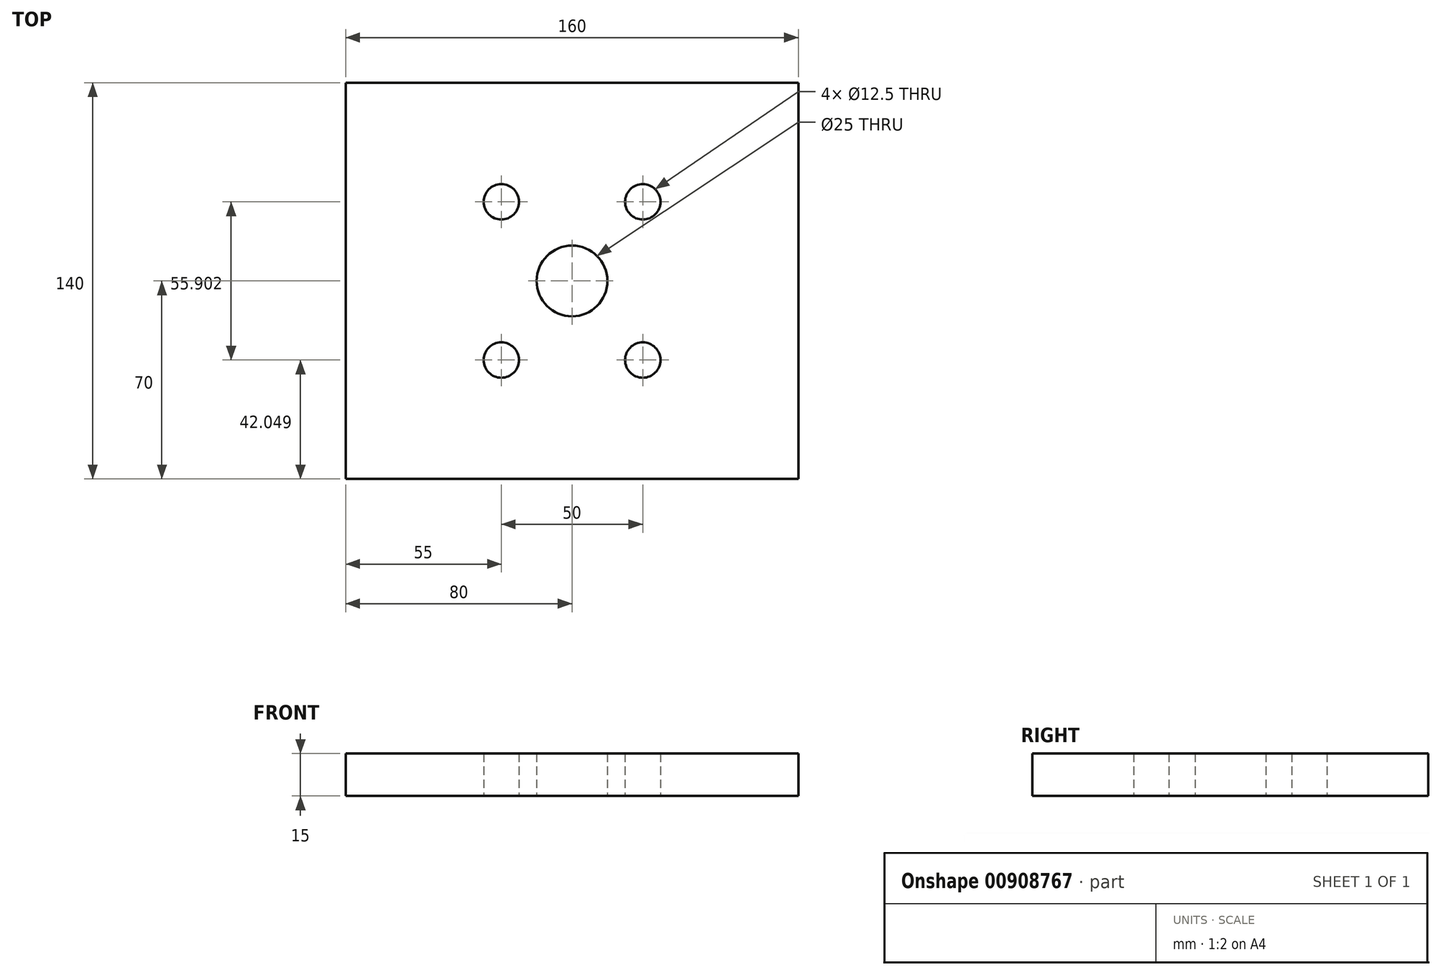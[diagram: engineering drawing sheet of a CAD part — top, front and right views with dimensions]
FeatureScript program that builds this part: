
annotation { "Feature Type Name" : "Feature", "Feature Type Description" : "" }
export const myFeature = defineFeature(function(context is Context, id is Id, definition is map)
    precondition{}
    {
        {
            var Q0;
            Q0=qCreatedBy(makeId("Top.planeOp"),FACE);
            var sketch = newSketch(context, id + "F0", { "sketchPlane" : qUnion([Q0])});
            skPoint(sketch, "E0", {"position": v(0, 50) * mm});
            skPoint(sketch, "E1", {"position": v(50, 0) * mm});
            skSolve(sketch);
        }
        {
            var Q0;
            Q0=qCreatedBy(makeId("Front.planeOp"),FACE);
            var sketch = newSketch(context, id + "F1", { "sketchPlane" : qUnion([Q0])});
            skPoint(sketch, "E2", {"position": v(0, 50) * mm});
            skSolve(sketch);
        }
        {
            var Q0;
            Q0=qCreatedBy(makeId("Top.planeOp"),FACE);
            var sketch = newSketch(context, id + "F2", { "sketchPlane" : qUnion([Q0])});
            skLineSegment(sketch, "E3.bottom", {"start": v(80, 70) * mm, "end": v(-80, 70) * mm});
            skLineSegment(sketch, "E3.top", {"start": v(80, -70) * mm, "end": v(-80, -70) * mm});
            skLineSegment(sketch, "E3.left", {"start": v(80, 70) * mm, "end": v(80, -70) * mm});
            skLineSegment(sketch, "E3.right", {"start": v(-80, 70) * mm, "end": v(-80, -70) * mm});
            skPoint(sketch, "E3.middle", {"position": v(0, 0) * mm});
            skCircle(sketch, "E4", {"center": v(0, 0) * mm, "radius": 12.5 * mm});
            skCircle(sketch, "E5", {"center": v(0, 0) * mm, "radius": 37.5 * mm, "construction": true});
            skCircle(sketch, "E6", {"center": v(-25, 27.95) * mm, "radius": 6.25 * mm});
            skCircle(sketch, "E7.MirrorC", {"center": v(-25, -27.95) * mm, "radius": 6.25 * mm});
            skCircle(sketch, "E8.MirrorC", {"center": v(25, 27.95) * mm, "radius": 6.25 * mm});
            skCircle(sketch, "E9.MirrorC", {"center": v(25, -27.95) * mm, "radius": 6.25 * mm});
            skLineSegment(sketch, "E10", {"start": v(-25, 27.95) * mm, "end": v(-25, -27.95) * mm, "construction": true});
            skLineSegment(sketch, "E11", {"start": v(-25, 27.95) * mm, "end": v(25, 27.95) * mm, "construction": true});
            skLineSegment(sketch, "E12", {"start": v(0, 0) * mm, "end": v(-12.5, 0) * mm, "construction": true});
            skLineSegment(sketch, "E13", {"start": v(-12.5, 0) * mm, "end": v(-25, 0) * mm, "construction": true});
            skLineSegment(sketch, "E14", {"start": v(-25, 0) * mm, "end": v(-37.5, 0) * mm, "construction": true});
            skCircle(sketch, "E15.0.1.0", {"center": v(-93, 226.95) * mm, "radius": 6.25 * mm});
            skCircle(sketch, "E15.0.1.1", {"center": v(-68, 199) * mm, "radius": 12.5 * mm});
            skCircle(sketch, "E15.0.1.2", {"center": v(-43, 226.95) * mm, "radius": 6.25 * mm});
            skCircle(sketch, "E15.0.1.3", {"center": v(-43, 171.05) * mm, "radius": 6.25 * mm});
            skCircle(sketch, "E15.0.1.4", {"center": v(-93, 171.05) * mm, "radius": 6.25 * mm});
            skCircle(sketch, "E15.0.2.0", {"center": v(-161, 425.95) * mm, "radius": 6.25 * mm});
            skCircle(sketch, "E15.0.2.1", {"center": v(-136, 398) * mm, "radius": 12.5 * mm});
            skCircle(sketch, "E15.0.2.2", {"center": v(-111, 425.95) * mm, "radius": 6.25 * mm});
            skCircle(sketch, "E15.0.2.3", {"center": v(-111, 370.05) * mm, "radius": 6.25 * mm});
            skCircle(sketch, "E15.0.2.4", {"center": v(-161, 370.05) * mm, "radius": 6.25 * mm});
            skCircle(sketch, "E15.1.0.0", {"center": v(184.5, -40.16) * mm, "radius": 6.25 * mm});
            skCircle(sketch, "E15.1.0.1", {"center": v(209.5, -68.11) * mm, "radius": 12.5 * mm});
            skCircle(sketch, "E15.1.0.2", {"center": v(234.5, -40.16) * mm, "radius": 6.25 * mm});
            skCircle(sketch, "E15.1.0.3", {"center": v(234.5, -96.06) * mm, "radius": 6.25 * mm});
            skCircle(sketch, "E15.1.0.4", {"center": v(184.5, -96.06) * mm, "radius": 6.25 * mm});
            skCircle(sketch, "E15.1.1.0", {"center": v(116.5, 158.84) * mm, "radius": 6.25 * mm});
            skCircle(sketch, "E15.1.1.1", {"center": v(141.5, 130.89) * mm, "radius": 12.5 * mm});
            skCircle(sketch, "E15.1.1.2", {"center": v(166.5, 158.84) * mm, "radius": 6.25 * mm});
            skCircle(sketch, "E15.1.1.3", {"center": v(166.5, 102.94) * mm, "radius": 6.25 * mm});
            skCircle(sketch, "E15.1.1.4", {"center": v(116.5, 102.94) * mm, "radius": 6.25 * mm});
            skCircle(sketch, "E15.1.2.0", {"center": v(48.5, 357.84) * mm, "radius": 6.25 * mm});
            skCircle(sketch, "E15.1.2.1", {"center": v(73.5, 329.89) * mm, "radius": 12.5 * mm});
            skCircle(sketch, "E15.1.2.2", {"center": v(98.5, 357.84) * mm, "radius": 6.25 * mm});
            skCircle(sketch, "E15.1.2.3", {"center": v(98.5, 301.94) * mm, "radius": 6.25 * mm});
            skCircle(sketch, "E15.1.2.4", {"center": v(48.5, 301.94) * mm, "radius": 6.25 * mm});
            skCircle(sketch, "E15.2.0.0", {"center": v(394, -108.27) * mm, "radius": 6.25 * mm});
            skCircle(sketch, "E15.2.0.1", {"center": v(419, -136.22) * mm, "radius": 12.5 * mm});
            skCircle(sketch, "E15.2.0.2", {"center": v(444, -108.27) * mm, "radius": 6.25 * mm});
            skCircle(sketch, "E15.2.0.3", {"center": v(444, -164.17) * mm, "radius": 6.25 * mm});
            skCircle(sketch, "E15.2.0.4", {"center": v(394, -164.17) * mm, "radius": 6.25 * mm});
            skCircle(sketch, "E15.2.1.0", {"center": v(326, 90.73) * mm, "radius": 6.25 * mm});
            skCircle(sketch, "E15.2.1.1", {"center": v(351, 62.78) * mm, "radius": 12.5 * mm});
            skCircle(sketch, "E15.2.1.2", {"center": v(376, 90.73) * mm, "radius": 6.25 * mm});
            skCircle(sketch, "E15.2.1.3", {"center": v(376, 34.83) * mm, "radius": 6.25 * mm});
            skCircle(sketch, "E15.2.1.4", {"center": v(326, 34.83) * mm, "radius": 6.25 * mm});
            skCircle(sketch, "E15.2.2.0", {"center": v(258, 289.73) * mm, "radius": 6.25 * mm});
            skCircle(sketch, "E15.2.2.1", {"center": v(283, 261.78) * mm, "radius": 12.5 * mm});
            skCircle(sketch, "E15.2.2.2", {"center": v(308, 289.73) * mm, "radius": 6.25 * mm});
            skCircle(sketch, "E15.2.2.3", {"center": v(308, 233.83) * mm, "radius": 6.25 * mm});
            skCircle(sketch, "E15.2.2.4", {"center": v(258, 233.83) * mm, "radius": 6.25 * mm});
            skCircle(sketch, "E15.3.0.0", {"center": v(603.5, -176.38) * mm, "radius": 6.25 * mm});
            skCircle(sketch, "E15.3.0.1", {"center": v(628.5, -204.33) * mm, "radius": 12.5 * mm});
            skCircle(sketch, "E15.3.0.2", {"center": v(653.5, -176.38) * mm, "radius": 6.25 * mm});
            skCircle(sketch, "E15.3.0.3", {"center": v(653.5, -232.28) * mm, "radius": 6.25 * mm});
            skCircle(sketch, "E15.3.0.4", {"center": v(603.5, -232.28) * mm, "radius": 6.25 * mm});
            skCircle(sketch, "E15.3.1.0", {"center": v(535.5, 22.62) * mm, "radius": 6.25 * mm});
            skCircle(sketch, "E15.3.1.1", {"center": v(560.5, -5.33) * mm, "radius": 12.5 * mm});
            skCircle(sketch, "E15.3.1.2", {"center": v(585.5, 22.62) * mm, "radius": 6.25 * mm});
            skCircle(sketch, "E15.3.1.3", {"center": v(585.5, -33.28) * mm, "radius": 6.25 * mm});
            skCircle(sketch, "E15.3.1.4", {"center": v(535.5, -33.28) * mm, "radius": 6.25 * mm});
            skCircle(sketch, "E15.3.2.0", {"center": v(467.5, 221.62) * mm, "radius": 6.25 * mm});
            skCircle(sketch, "E15.3.2.1", {"center": v(492.5, 193.67) * mm, "radius": 12.5 * mm});
            skCircle(sketch, "E15.3.2.2", {"center": v(517.5, 221.62) * mm, "radius": 6.25 * mm});
            skCircle(sketch, "E15.3.2.3", {"center": v(517.5, 165.72) * mm, "radius": 6.25 * mm});
            skCircle(sketch, "E15.3.2.4", {"center": v(467.5, 165.72) * mm, "radius": 6.25 * mm});
            skCircle(sketch, "E15.4.0.0", {"center": v(813, -244.5) * mm, "radius": 6.25 * mm});
            skCircle(sketch, "E15.4.0.1", {"center": v(838, -272.44) * mm, "radius": 12.5 * mm});
            skCircle(sketch, "E15.4.0.2", {"center": v(863, -244.5) * mm, "radius": 6.25 * mm});
            skCircle(sketch, "E15.4.0.3", {"center": v(863, -300.4) * mm, "radius": 6.25 * mm});
            skCircle(sketch, "E15.4.0.4", {"center": v(813, -300.4) * mm, "radius": 6.25 * mm});
            skCircle(sketch, "E15.4.1.0", {"center": v(745, -45.5) * mm, "radius": 6.25 * mm});
            skCircle(sketch, "E15.4.1.1", {"center": v(770, -73.44) * mm, "radius": 12.5 * mm});
            skCircle(sketch, "E15.4.1.2", {"center": v(795, -45.5) * mm, "radius": 6.25 * mm});
            skCircle(sketch, "E15.4.1.3", {"center": v(795, -101.4) * mm, "radius": 6.25 * mm});
            skCircle(sketch, "E15.4.1.4", {"center": v(745, -101.4) * mm, "radius": 6.25 * mm});
            skCircle(sketch, "E15.4.2.0", {"center": v(677, 153.5) * mm, "radius": 6.25 * mm});
            skCircle(sketch, "E15.4.2.1", {"center": v(702, 125.56) * mm, "radius": 12.5 * mm});
            skCircle(sketch, "E15.4.2.2", {"center": v(727, 153.5) * mm, "radius": 6.25 * mm});
            skCircle(sketch, "E15.4.2.3", {"center": v(727, 97.6) * mm, "radius": 6.25 * mm});
            skCircle(sketch, "E15.4.2.4", {"center": v(677, 97.6) * mm, "radius": 6.25 * mm});
            skLineSegment(sketch, "E15.direction1", {"start": v(0, 0) * mm, "end": v(209.5, -68.11) * mm, "construction": true});
            skLineSegment(sketch, "E15.direction2", {"start": v(0, 0) * mm, "end": v(-68, 199) * mm, "construction": true});
            skSolve(sketch);
        }
        {
            var Q0;
            Q0=makeQuery(id+"F2.imprint","IMPRINT",FACE,{"disambiguationData":[TD([[makeQuery(id+"F2.imprint","IMPRINT",EDGE,{"derivedFrom":sQuery(id+"F2.wireOp",EDGE,"E3.bottom")}),1.0]])]});
            extrude(context, id + "F3", {"entities" : qUnion([Q0]), "depth" : 15 * mm, "offsetDistance" : 25 * mm});
        }
    });
